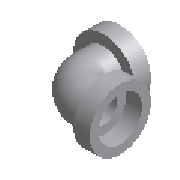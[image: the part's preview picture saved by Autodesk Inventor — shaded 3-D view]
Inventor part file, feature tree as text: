
AUTODESK INVENTOR PART (.ipt)
format: ipt  version: 2025 (Build 290162000, 162)  size: 216,064 bytes
history: native  units: mm (DEFAULTED — no unit token found)
features: other x6, revolve x2, sweep x1
ambient origin geometry x8: Origin, YZ Plane, XZ Plane, XY Plane, X Axis, Y Axis, Z Axis, Center Point
bodies: Solid1 (feature_tree)
feature tree (9):
  revolve  "Revolve1"  [1 undecoded]
  sweep  "Sweep1"
  revolve  "Revolve2"  [1 undecoded]
  other  "Work Axis1"
  other  "Work Point1"
  other  "Work Point2"
  other  "Work Axis2"
  other  "Work Point3"
  other  "Work Point4"
note: 2 required parameter values undecoded (feature->parameter linkage not recoverable at this tier; creation-order binding heuristic only, values carry confidence <= 0.55)
